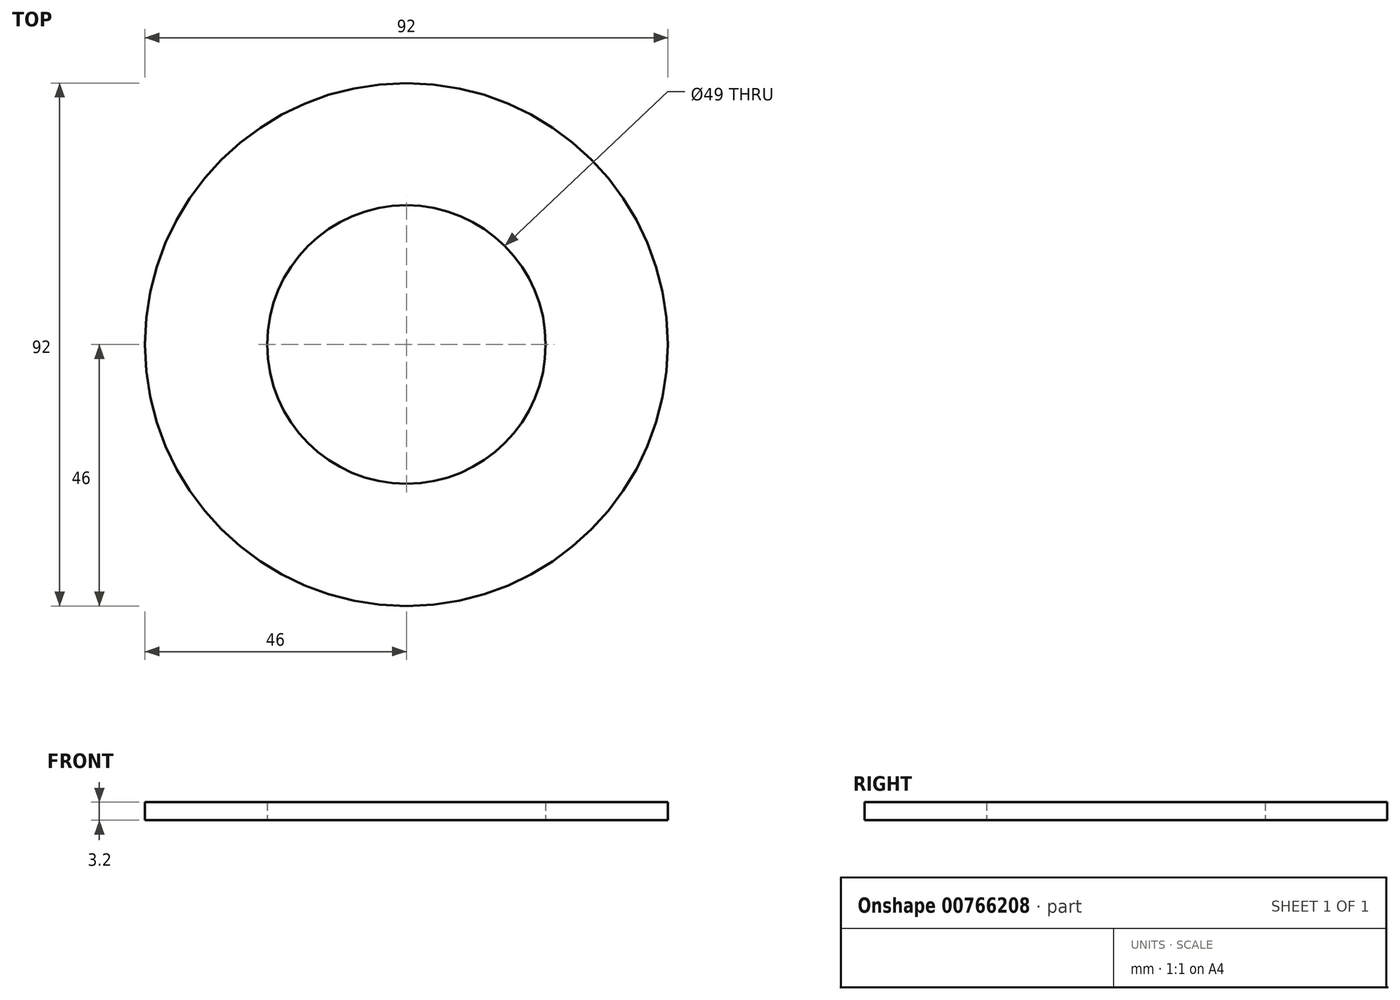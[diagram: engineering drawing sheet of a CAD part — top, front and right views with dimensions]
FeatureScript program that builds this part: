
annotation { "Feature Type Name" : "Feature", "Feature Type Description" : "" }
export const myFeature = defineFeature(function(context is Context, id is Id, definition is map)
    precondition{}
    {
        {
            var Q0;
            Q0=qCreatedBy(makeId("Top.planeOp"),FACE);
            var sketch = newSketch(context, id + "F0", { "sketchPlane" : qUnion([Q0])});
            skCircle(sketch, "E0", {"center": v(0, 0) * mm, "radius": 46 * mm});
            skCircle(sketch, "E1", {"center": v(0, 0) * mm, "radius": 24.5 * mm});
            skSolve(sketch);
        }
        {
            var Q0;
            Q0 = qSketchRegion(id + "F0", true);
            extrude(context, id + "F1", {"entities" : qUnion([Q0]), "depth" : 3.2 * mm, "offsetDistance" : 25 * mm});
        }
    });
